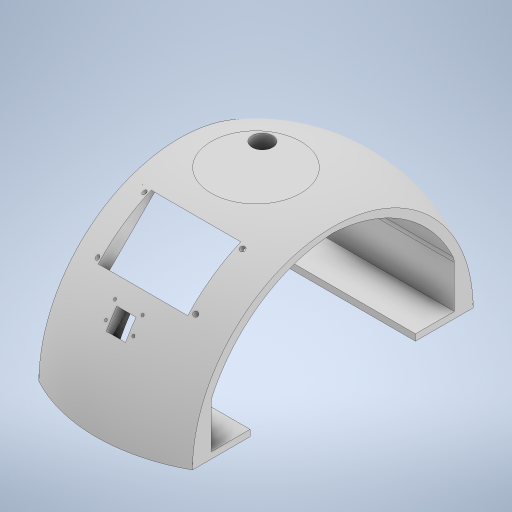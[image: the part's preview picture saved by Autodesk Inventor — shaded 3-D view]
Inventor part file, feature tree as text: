
AUTODESK INVENTOR PART (.ipt)
format: ipt  version: 2023 (Build 270158000, 158)  size: 482,304 bytes
history: native  units: mm
features: sketch x14, extrude x11, fillet x3, hole x2, other x1, revolve x1
ambient origin geometry x8: Origin, YZ Plane, XZ Plane, XY Plane, X Axis, Y Axis, Z Axis, Center Point
bodies: Body1 (feature_tree)
feature tree (32):
  other  "ソリッド1"
  revolve  "回転1"
  extrude  "押し出し1"  Depth=125.0mm
  extrude  "押し出し2"  TaperAngle=180.0deg  [1 undecoded]
  extrude  "押し出し3"  TaperAngle=45.0deg  [1 undecoded]
  extrude  "押し出し4"  Depth=125.0mm
  extrude  "押し出し5"  Depth=120.0mm
  hole  "穴1"  [1 undecoded]
  extrude  "押し出し6"  TaperAngle=90.0deg  [1 undecoded]
  extrude  "押し出し7"  Depth=120.0mm
  fillet  "フィレット1"  Radius=250.0mm
  fillet  "フィレット2"  Radius=200.0mm
  extrude  "押し出し8"  TaperAngle=135.0deg  [1 undecoded]
  hole  "穴2"  [1 undecoded]
  extrude  "押し出し9"  Depth=70.0mm
  extrude  "押し出し10"  Depth=50.0mm
  extrude  "押し出し11"  Depth=60.0mm
  fillet  "フィレット3"  Radius=20.0mm
  sketch  "スケッチ1"
  sketch  "スケッチ2"
  sketch  "スケッチ3"
  sketch  "スケッチ4"
  sketch  "スケッチ5"
  sketch  "スケッチ6"
  sketch  "スケッチ7"
  sketch  "スケッチ8"
  sketch  "スケッチ9"
  sketch  "スケッチ11"
  sketch  "スケッチ12"
  sketch  "スケッチ13"
  sketch  "スケッチ14"
  sketch  "スケッチ15"
note: 6 required parameter values undecoded (feature->parameter linkage not recoverable at this tier; creation-order binding heuristic only, values carry confidence <= 0.55)
